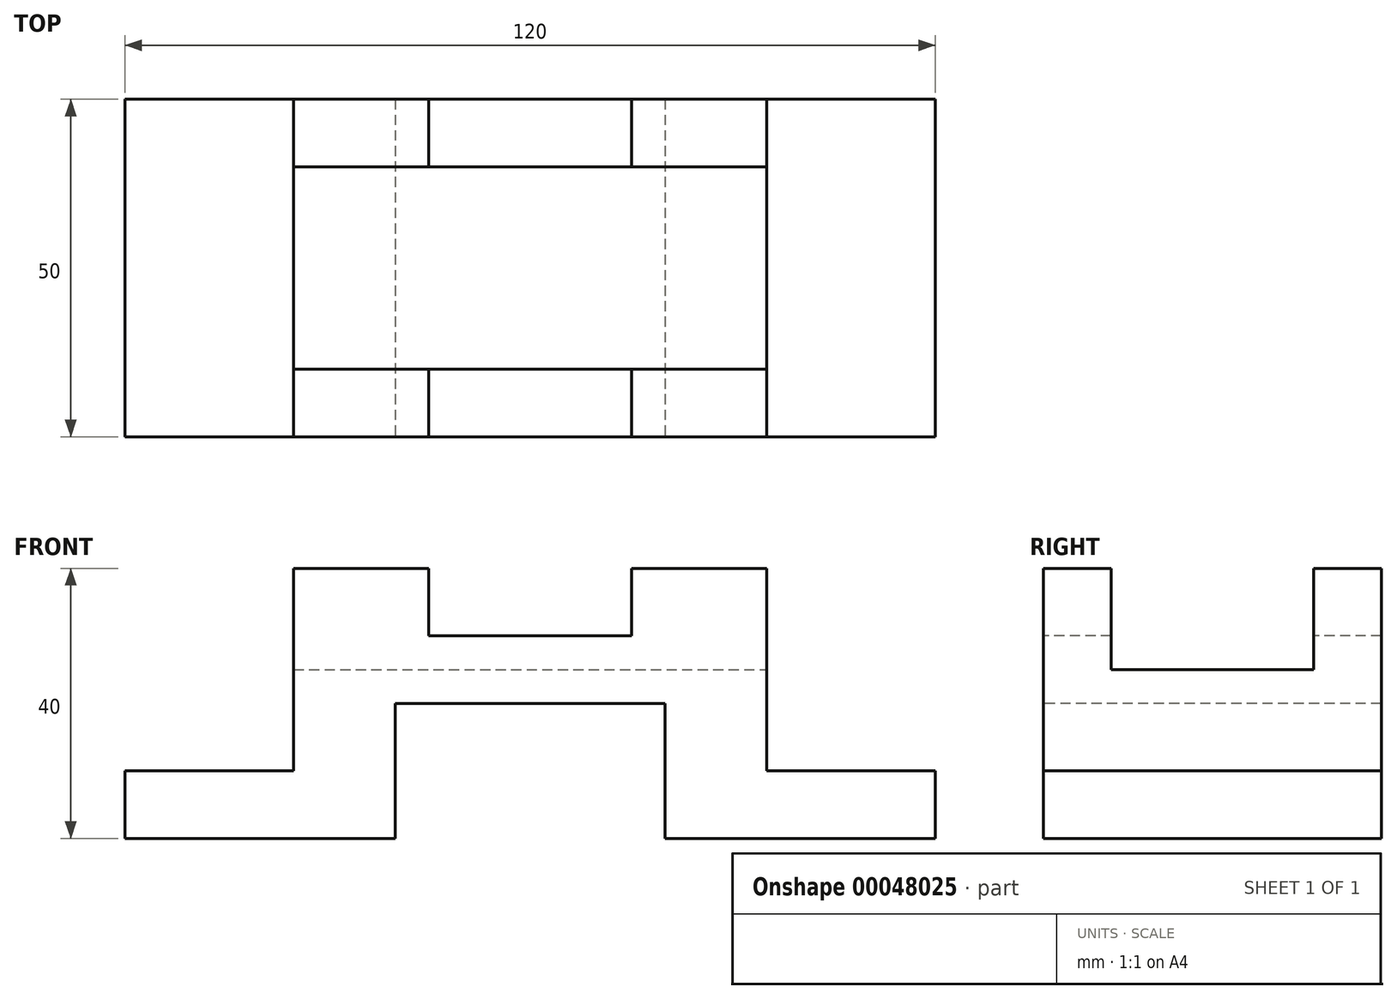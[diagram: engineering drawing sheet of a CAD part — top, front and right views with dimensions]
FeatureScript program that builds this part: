
annotation { "Feature Type Name" : "Feature", "Feature Type Description" : "" }
export const myFeature = defineFeature(function(context is Context, id is Id, definition is map)
    precondition{}
    {
        {
            assignVariable(context, id + "F0", {"name" : "A", "anyValue" : 50});
        }
        {
            var Q0;
            Q0=qCreatedBy(makeId("Front.planeOp"),FACE);
            var sketch = newSketch(context, id + "F1", { "sketchPlane" : qUnion([Q0])});
            skLineSegment(sketch, "E0", {"start": v(0, 0) * mm, "end": v(0, 20) * mm});
            skLineSegment(sketch, "E1", {"start": v(0, 20) * mm, "end": v(-40, 20) * mm});
            skLineSegment(sketch, "E2", {"start": v(-40, 20) * mm, "end": v(-40, 0) * mm});
            skLineSegment(sketch, "E3", {"start": v(-40, 0) * mm, "end": v(-80, 0) * mm});
            skLineSegment(sketch, "E4", {"start": v(-80, 0) * mm, "end": v(-80, 10) * mm});
            skLineSegment(sketch, "E5", {"start": v(-80, 10) * mm, "end": v(-55, 10) * mm});
            skLineSegment(sketch, "E6", {"start": v(-55, 10) * mm, "end": v(-55, 40) * mm});
            skLineSegment(sketch, "E7", {"start": v(-55, 40) * mm, "end": v(-35, 40) * mm});
            skLineSegment(sketch, "E8", {"start": v(-35, 40) * mm, "end": v(-35, 30) * mm});
            skLineSegment(sketch, "E9", {"start": v(-35, 30) * mm, "end": v(-5, 30) * mm});
            skLineSegment(sketch, "E10", {"start": v(-5, 30) * mm, "end": v(-5, 40) * mm});
            skLineSegment(sketch, "E11", {"start": v(-5, 40) * mm, "end": v(15, 40) * mm});
            skLineSegment(sketch, "E12", {"start": v(15, 40) * mm, "end": v(15, 10) * mm});
            skLineSegment(sketch, "E13", {"start": v(15, 10) * mm, "end": v(40, 10) * mm});
            skLineSegment(sketch, "E14", {"start": v(40, 10) * mm, "end": v(40, 0) * mm});
            skLineSegment(sketch, "E15", {"start": v(40, 0) * mm, "end": v(0, 0) * mm});
            skSolve(sketch);
        }
        {
            var Q0;
            Q0 = qSketchRegion(id + "F1", true);
            extrude(context, id + "F2", {"entities" : qUnion([Q0]), "oppositeDirection" : true, "depth" : (getVariable(context, 'A')) * mm});
        }
        {
            var Q0;
            Q0=makeQuery(id+"F2.opExtrude","SWEPT_FACE",FACE,{"disambiguationData":[OSD([sQuery(id+"F1.wireOp",EDGE,"E12")])]});
            var sketch = newSketch(context, id + "F3", { "sketchPlane" : qUnion([Q0])});
            skLineSegment(sketch, "E16.bottom", {"start": v(10, 40) * mm, "end": v(40, 40) * mm});
            skLineSegment(sketch, "E16.top", {"start": v(10, 25) * mm, "end": v(40, 25) * mm});
            skLineSegment(sketch, "E16.left", {"start": v(10, 40) * mm, "end": v(10, 25) * mm});
            skLineSegment(sketch, "E16.right", {"start": v(40, 40) * mm, "end": v(40, 25) * mm});
            skSolve(sketch);
        }
        {
            var Q0;
            Q0=makeQuery(id+"F3.imprint","IMPRINT",FACE,{"disambiguationData":[TD([[makeQuery(id+"F3.imprint","IMPRINT",EDGE,{"derivedFrom":sQuery(id+"F3.wireOp",EDGE,"E16.bottom")}),1.0]])]});
            extrude(context, id + "F4", {"entities" : qUnion([Q0]), "operationType" : NewBodyOperationType.REMOVE, "oppositeDirection" : true, "depth" : 70 * mm});
        }
    });
